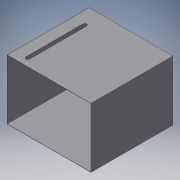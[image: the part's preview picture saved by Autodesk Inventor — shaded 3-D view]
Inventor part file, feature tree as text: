
AUTODESK INVENTOR PART (.ipt)
format: ipt  version: 2019 (Build 230136000, 136)  size: 362,496 bytes
history: native  units: in
note: dims shown in document units (in); Inventor stores cm internally (conversion verified against a paired STEP export)
features: extrude x10, sketch x10, projected_geometry x9, fillet x5, other x5, reference x4, helix x1
ambient origin geometry x8: Origin, YZ Plane, XZ Plane, XY Plane, X Axis, Y Axis, Z Axis, Center Point
bodies: Solid1 (feature_tree)
feature tree (44):
  extrude  "Extrusion1"  Depth=0.5906in
  extrude  "Extrusion2"  Depth=0.0472in
  fillet  "Fillet1"  Radius=0.0472in
  extrude  "Extrusion3"  Depth=11.811in
  fillet  "Fillet2"  Radius=0.7874in
  extrude  "Extrusion4"  Depth=5.5541in TaperAngle=0.0deg
  extrude  "Extrusion5"  Depth=0.0472in TaperAngle=0.0deg
  fillet  "Fillet3"  Radius=0.1969in
  extrude  "Extrusion6"  Depth=0.0472in
  extrude  "Extrusion7"  Depth=0.0472in TaperAngle=0.0deg
  extrude  "Extrusion8"  Depth=0.0472in TaperAngle=0.0deg
  extrude  "Extrusion9"  Depth=0.0472in TaperAngle=0.0deg
  extrude  "Extrusion10"  Depth=0.0472in TaperAngle=0.0deg
  fillet  "Fillet4"  Radius=0.0472in
  fillet  "Fillet5"  Radius=0.0787in
  sketch  "Sketch1"  dims[d0=0.5906in d1=0.5906in]
  reference  "Reference1"
  reference  "Reference2"
  reference  "Reference3"
  reference  "Reference4"
  sketch  "Sketch2"  dims[d2=0.5906in d3=0.5906in d4=0.0472in]
  sketch  "Sketch3"  dims[d5=16.9291in d6=0.0in d7=11.811in d8=0.7874in]
  projected_geometry  "Projected Loop1"
  sketch  "Sketch4"  dims[d9=1.5748in d10=5.5541in d11=0.0in]
  projected_geometry  "Projected Loop2"
  sketch  "Sketch5"  dims[d12=0.1969in d13=0.0472in d14=0.0in d15=0.1969in]
  projected_geometry  "Projected Loop3"
  projected_geometry  "Projected Loop4"
  sketch  "Sketch6"  dims[d16=0.7874in d17=0.0472in]
  projected_geometry  "Projected Loop5"
  sketch  "Sketch7"  dims[d18=1.1811in d19=0.0in d20=0.0472in d21=0.0in]
  projected_geometry  "Projected Loop6"
  sketch  "Sketch8"  dims[d22=0.1969in d23=0.0472in d24=0.0in]
  projected_geometry  "Projected Loop7"
  sketch  "Sketch9"  dims[d25=60.0deg d26=0.0472in d27=0.0in]
  projected_geometry  "Projected Loop8"
  sketch  "Sketch10"  dims[d28=0.0472in d29=0.0in d30=0.0472in d31=0.0in d32=0.0472in d33=0.0in d34=0.0787in d35=0.0787in]
  projected_geometry  "Projected Loop9"
  other  "Assembly3"
  helix  "Helix DLP Z Stage:1"  [1 undecoded]
  other  "Z stage_side:2"
  other  "Z stage_side:1"
  other  "Print Platform:1"
  other  "Z stage_brace:1"
note: 1 required parameter value undecoded (feature->parameter linkage not recoverable at this tier; creation-order binding heuristic only, values carry confidence <= 0.55)
